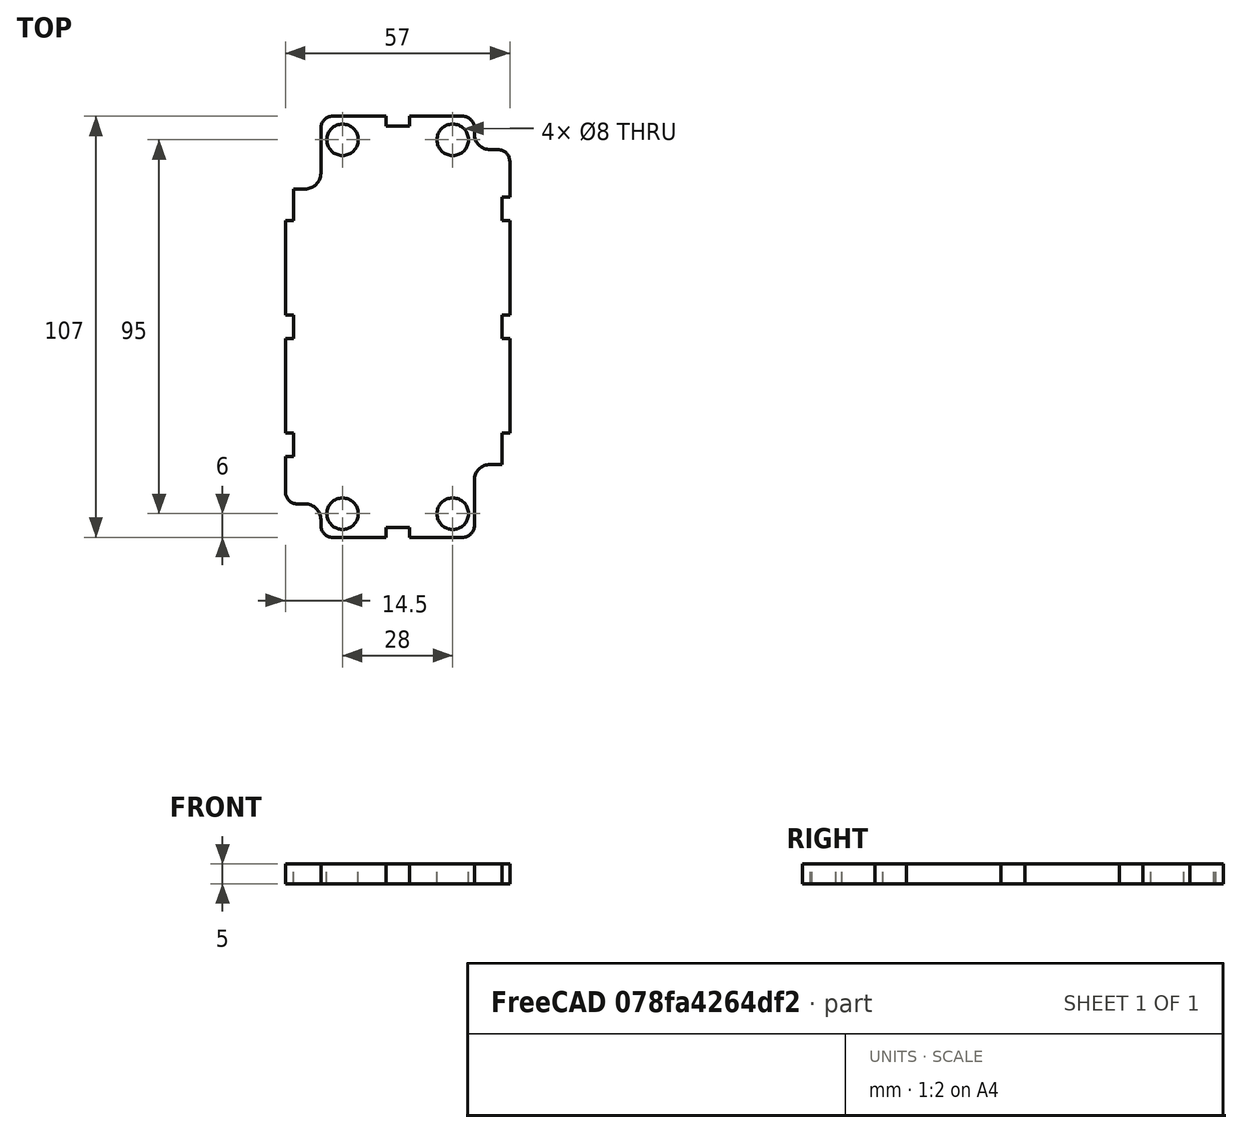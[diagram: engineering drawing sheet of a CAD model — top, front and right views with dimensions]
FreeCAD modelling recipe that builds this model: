
FCSTD DOCUMENT  (FreeCAD 0.16R)
Label: supportSigfox4
License: All rights reserved
LicenseURL: http://en.wikipedia.org/wiki/All_rights_reserved
objects: Part::Box×13, Part::Cylinder×4, PartDesign::Fillet×2, Part::MultiFuse×1, Part::Cut×1
note: 21 computed .brp shape members not serialized (recipe doc carries the construction recipe); baked Part::Feature solids carry a one-line shape summary decoded from their .brp

FEATURE [Part::Box] Box  label="Cube"
  Height = 5
  Length = 57
  Placement = pos=(0,0.5,0) rot=(0,0,1;0rad)
  Width = 107
FEATURE [Part::Box] Box001  label="Cube001"
  Height = 10
  Length = 9
  Placement = pos=(48,0,0) rot=(0,0,1;0rad)
  Width = 19
FEATURE [Part::Box] Box002  label="Cube002"
  Height = 10
  Length = 9
  Width = 9
FEATURE [Part::Box] Box003  label="Cube003"
  Height = 10
  Length = 9
  Placement = pos=(0,89,0) rot=(0,0,1;0rad)
  Width = 19
FEATURE [Part::Box] Box004  label="Cube004"
  Height = 10
  Length = 9
  Placement = pos=(48,99,0) rot=(0,0,1;0rad)
  Width = 9
FEATURE [Part::Box] Box005  label="Cube005"
  Height = 10
  Length = 2
  Placement = pos=(0,51,0) rot=(0,0,1;0rad)
  Width = 6
FEATURE [Part::Box] Box006  label="Cube006"
  Height = 10
  Length = 2
  Placement = pos=(0,81,0) rot=(0,0,1;0rad)
  Width = 8
FEATURE [Part::Box] Box007  label="Cube007"
  Height = 10
  Length = 2
  Placement = pos=(0,21,0) rot=(0,0,1;0rad)
  Width = 6
FEATURE [Part::Box] Box008  label="Cube008"
  Height = 10
  Length = 2
  Placement = pos=(55,51,0) rot=(0,0,1;0rad)
  Width = 6
FEATURE [Part::Box] Box009  label="Cube009"
  Height = 10
  Length = 2
  Placement = pos=(55,81,0) rot=(0,0,1;0rad)
  Width = 6
FEATURE [Part::Box] Box010  label="Cube010"
  Height = 10
  Length = 2
  Placement = pos=(55,19,0) rot=(0,0,1;0rad)
  Width = 8
FEATURE [Part::Cylinder] Cylinder
  Angle = 360
  Height = 10
  Placement = pos=(14.5,6.5,0) rot=(0,0,1;0rad)
  Radius = 4
FEATURE [Part::Cylinder] Cylinder001
  Angle = 360
  Height = 10
  Placement = pos=(42.5,6.5,0) rot=(0,0,1;0rad)
  Radius = 4
FEATURE [Part::Cylinder] Cylinder002
  Angle = 360
  Height = 10
  Placement = pos=(42.5,101.5,0) rot=(0,0,1;0rad)
  Radius = 4
FEATURE [Part::Cylinder] Cylinder003
  Angle = 360
  Height = 10
  Placement = pos=(14.5,101.5,0) rot=(0,0,1;0rad)
  Radius = 4
FEATURE [Part::Box] Box011  label="Cube011"
  Height = 10
  Length = 3
  Placement = pos=(31.5,0,0) rot=(0,0,1;1.5708rad)
  Width = 6
FEATURE [Part::Box] Box012  label="Cube012"
  Height = 10
  Length = 3
  Placement = pos=(31.5,105,0) rot=(0,0,1;1.5708rad)
  Width = 6
FEATURE [Part::MultiFuse] Fusion
  Shapes = -> [Box001,Box002,Box003,Box004,Box005,Box006,Box007,Box008,Box009,Box010,Cylinder,Cylinder002,Cylinder001,Cylinder003,Box011,Box012]
FEATURE [Part::Cut] Cut
  Base = -> Box
  Tool = -> Fusion
FEATURE [PartDesign::Fillet] Fillet
  Base = -> Cut [Edge103,Edge108,Edge110,Edge123,Edge128,Edge4]
  Radius = 3
FEATURE [PartDesign::Fillet] Fillet001
  Base = -> Fillet [Edge124,Edge142,Edge105,Edge123]
  Radius = 4
